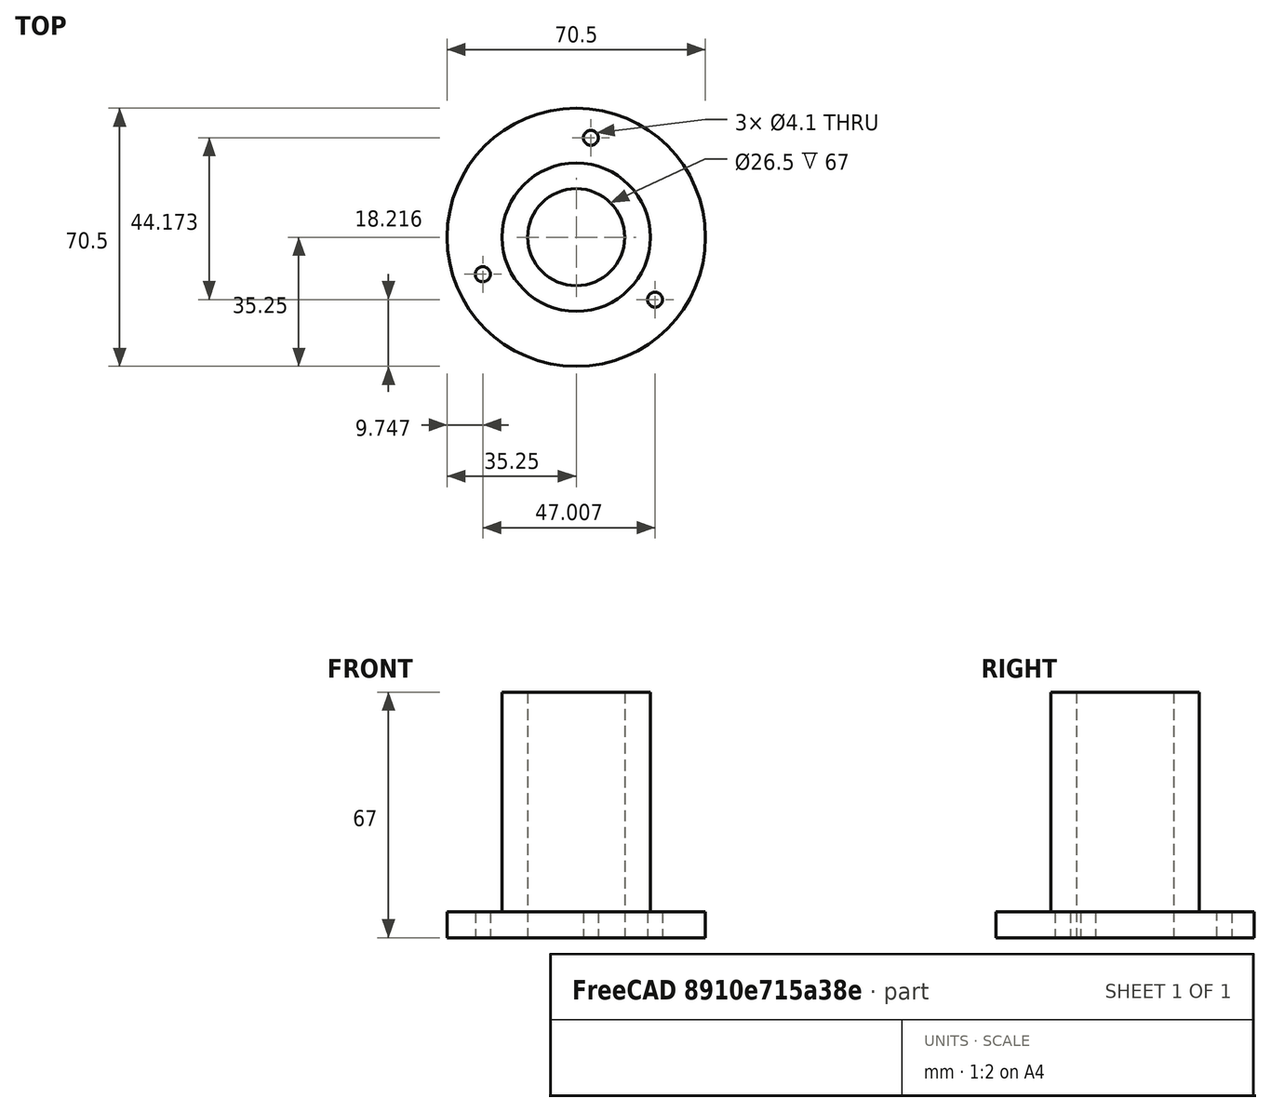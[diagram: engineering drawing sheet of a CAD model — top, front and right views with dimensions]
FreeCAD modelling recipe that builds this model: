
FCSTD DOCUMENT  (FreeCAD 1.1R38827 (Git))
Label: composit_stand3_sleeve_outer_main
License: All rights reserved
LicenseURL: http://en.wikipedia.org/wiki/All_rights_reserved
objects: Sketcher::SketchObject×1, Part::FeaturePython×1, Part::Feature×1
note: 4 computed .brp shape members not serialized (recipe doc carries the construction recipe); baked Part::Feature solids carry a one-line shape summary decoded from their .brp
EXTERNAL_REF file=composit_stand3_sleeve_inner_main.FCStd obj=Sketch

FEATURE [Sketcher::SketchObject] Sketch  label="sleeve_outer_base_sketch"
  ArcFitTolerance = 0
  FullyConstrained = true
  MakeInternals = false
  Placement = pos=(0,0,0) rot=(1,0,0;1.5708rad)
  expr: .Constraints.inner_r = <<composit_stand3_sleeve_inner_main>>#<<sleeve_inner_base_sketch>>.Constraints.outer_r + 0.25 mm
  sketch-geometry (6):
    g0: LineSegment StartX=13.25 StartY=67 StartZ=0 EndX=13.25 EndY=0 EndZ=0
    g1: LineSegment StartX=13.25 StartY=0 StartZ=0 EndX=35.25 EndY=0 EndZ=0
    g2: LineSegment StartX=35.25 StartY=0 StartZ=0 EndX=35.25 EndY=7 EndZ=0
    g3: LineSegment StartX=35.25 StartY=7 StartZ=0 EndX=20.25 EndY=7 EndZ=0
    g4: LineSegment StartX=20.25 StartY=7 StartZ=0 EndX=20.25 EndY=67 EndZ=0
    g5: LineSegment StartX=20.25 StartY=67 StartZ=0 EndX=13.25 EndY=67 EndZ=0
  constraints (19):
    c: PointOnObject(g0,g-1)
    c: Vertical(g0)
    c: Coincident(g0,g1)
    c: PointOnObject(g1,g-1)
    c: Coincident(g1,g2)
    c: Vertical(g2)
    c: Coincident(g2,g3)
    c: Horizontal(g3)
    c: Coincident(g3,g4)
    c: Vertical(g4)
    c: Coincident(g4,g5)
    c: Coincident(g5,g0)
    c: Horizontal(g5)
    c: DistanceY(g0,g0) = 67  'height'
    c: DistanceX(g0) = 13.25  'inner_r'
    c: DistanceX(g1) = 35.25  'base_r'
    c: DistanceX(g5,g5) = 7
    c: DistanceX(g1,g1) = 22
    c: DistanceY(g2) = 7
FEATURE [Part::FeaturePython] PolarArray  label="fix"  # WARN: FeaturePython — macro-defined, semantics opaque (R4)
  Alignment = 0
  AttacherType = Attacher::AttachEngine3D
  CellStart = A1
  Count = 3
  DistributionLaw = 0
  EndInclusive = false
  ExposePlacement = false
  FlipX = false
  FlipZ = false
  GeneratorMode = 0
  MarkerShape = 1
  MarkerSize = 0
  NumElements = 3
  OrientMode = 2
  Placement = pos=(0,0,10) rot=(1,0,0;3.14159rad)
  Radius = 25
  Reverse = false
  SpanEnd = 360
  SpanStart = 0
  Step = 120
  Type = lattice2PolarArray2.PolarArray
  UseArcRadius = false
  UseArcRange = 0
  VSGVersion = 1
  Values = 0.0 | 120.0 | 240.0
  ValuesSource = 2
  isLattice = 1
FEATURE [Part::Feature] Body170  label="sleeve_outer002"
  shape: bbox 70.5 x 70.5 x 67 mm, 9 faces (baked)
